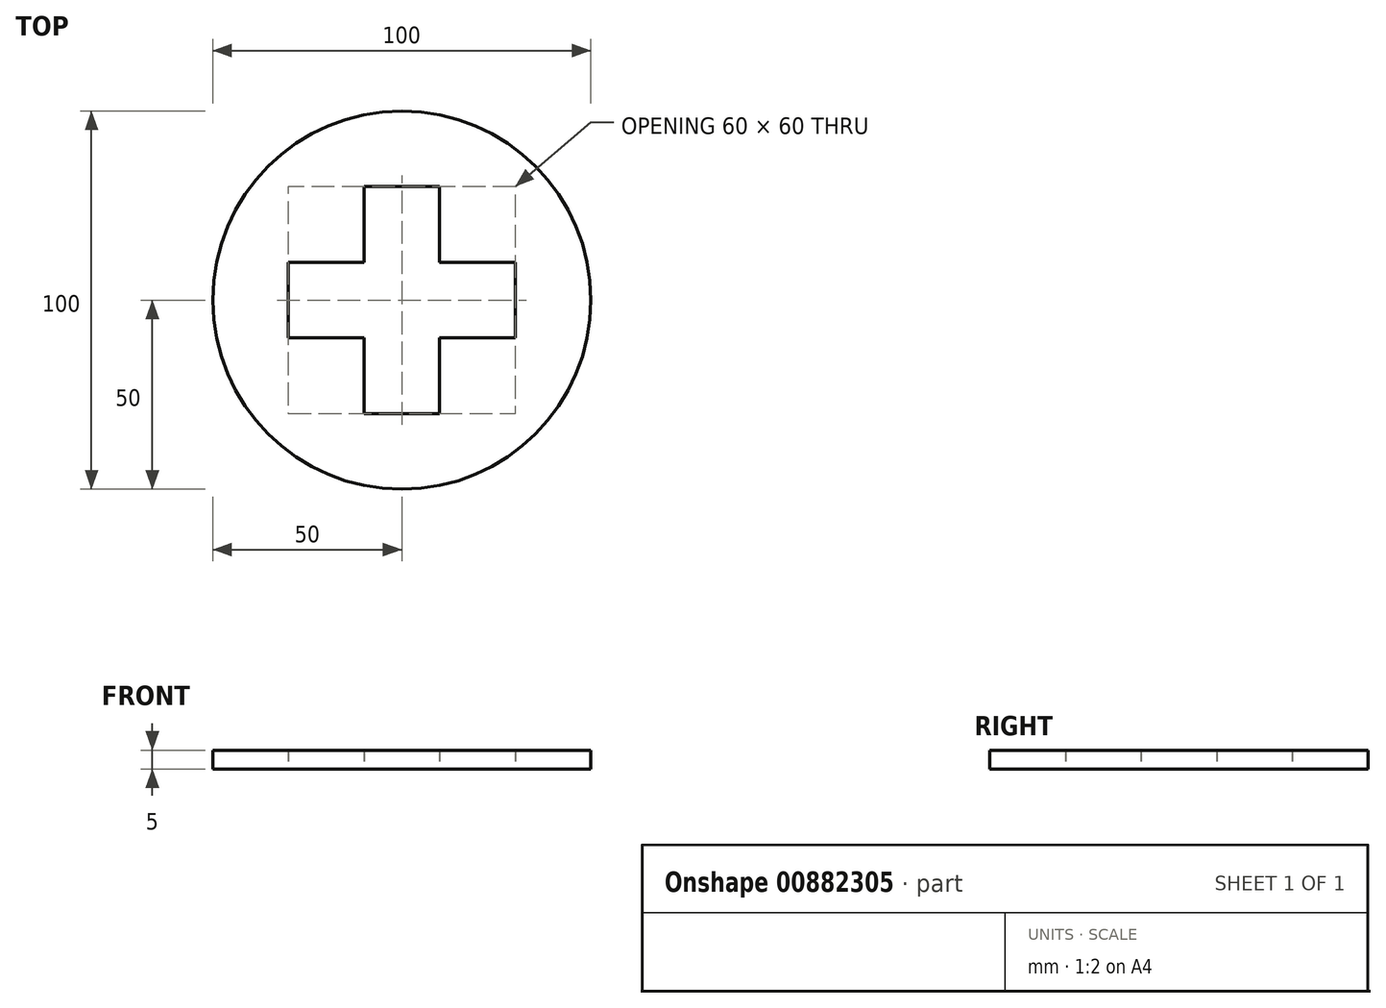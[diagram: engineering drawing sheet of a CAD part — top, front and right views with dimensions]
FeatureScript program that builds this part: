
annotation { "Feature Type Name" : "Feature", "Feature Type Description" : "" }
export const myFeature = defineFeature(function(context is Context, id is Id, definition is map)
    precondition{}
    {
        {
            var Q0;
            Q0=qCreatedBy(makeId("Top.planeOp"),FACE);
            var sketch = newSketch(context, id + "F0", { "sketchPlane" : qUnion([Q0])});
            skCircle(sketch, "E0", {"center": v(0, 0) * mm, "radius": 50 * mm});
            skLineSegment(sketch, "E1", {"start": v(0, 0) * mm, "end": v(-37.32, 0) * mm, "construction": true});
            skLineSegment(sketch, "E2", {"start": v(0, 0) * mm, "end": v(0, 42.9) * mm, "construction": true});
            skLineSegment(sketch, "E3", {"start": v(0, 30) * mm, "end": v(-10, 30) * mm});
            skLineSegment(sketch, "E4", {"start": v(-10, 30) * mm, "end": v(-10, 10) * mm});
            skLineSegment(sketch, "E5", {"start": v(-10, 10) * mm, "end": v(-30, 10) * mm});
            skLineSegment(sketch, "E6", {"start": v(-30, 10) * mm, "end": v(-30, 0) * mm});
            skLineSegment(sketch, "E7.MirrorCS", {"start": v(-30, -10) * mm, "end": v(-30, 0) * mm});
            skLineSegment(sketch, "E8.MirrorCS", {"start": v(-10, -10) * mm, "end": v(-30, -10) * mm});
            skLineSegment(sketch, "E9.MirrorCS", {"start": v(-10, -30) * mm, "end": v(-10, -10) * mm});
            skLineSegment(sketch, "E10.MirrorCS", {"start": v(0, -30) * mm, "end": v(-10, -30) * mm});
            skLineSegment(sketch, "E11.MirrorCS", {"start": v(0, 30) * mm, "end": v(10, 30) * mm});
            skLineSegment(sketch, "E12.MirrorCS", {"start": v(10, 30) * mm, "end": v(10, 10) * mm});
            skLineSegment(sketch, "E13.MirrorCS", {"start": v(10, 10) * mm, "end": v(30, 10) * mm});
            skLineSegment(sketch, "E14.MirrorCS", {"start": v(30, 10) * mm, "end": v(30, 0) * mm});
            skLineSegment(sketch, "E15.MirrorCS", {"start": v(30, -10) * mm, "end": v(30, 0) * mm});
            skLineSegment(sketch, "E16.MirrorCS", {"start": v(10, -10) * mm, "end": v(30, -10) * mm});
            skLineSegment(sketch, "E17.MirrorCS", {"start": v(10, -30) * mm, "end": v(10, -10) * mm});
            skLineSegment(sketch, "E18.MirrorCS", {"start": v(0, -30) * mm, "end": v(10, -30) * mm});
            skSolve(sketch);
        }
        {
            var Q0;
            Q0=qSketchRegion(id+"F0",true);
            extrude(context, id + "F1", {"entities" : qUnion([Q0]), "depth" : 5 * mm, "offsetDistance" : 25 * mm});
        }
    });
